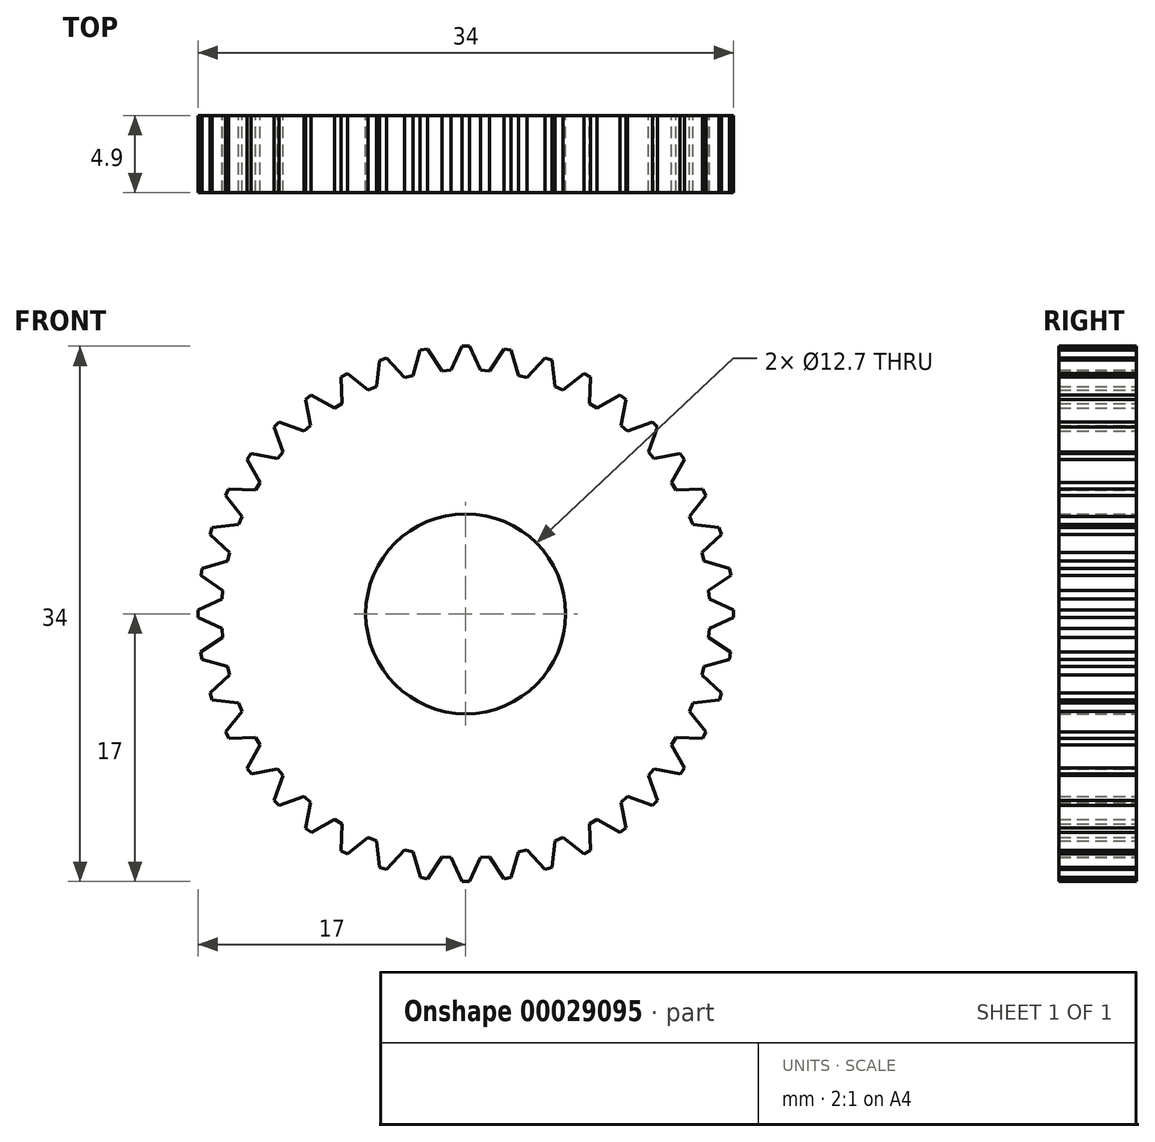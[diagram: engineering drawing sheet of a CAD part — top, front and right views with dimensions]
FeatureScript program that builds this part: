
annotation { "Feature Type Name" : "Feature", "Feature Type Description" : "" }
export const myFeature = defineFeature(function(context is Context, id is Id, definition is map)
    precondition{}
    {
        {
            var Q0;
            Q0=qCreatedBy(makeId("Front.planeOp"),FACE);
            var sketch = newSketch(context, id + "F0", { "sketchPlane" : qUnion([Q0])});
            skCircle(sketch, "E0", {"center": v(0, 0) * mm, "radius": 15 * mm, "construction": true});
            skCircle(sketch, "E1", {"center": v(0, 0) * mm, "radius": 15.5 * mm, "construction": true});
            skCircle(sketch, "E2", {"center": v(0, 0) * mm, "radius": 6.35 * mm});
            skCircle(sketch, "E3", {"center": v(0, 0) * mm, "radius": 17 * mm, "construction": true});
            skCircle(sketch, "E4", {"center": v(0, 0) * mm, "radius": 17.5 * mm, "construction": true});
            skLineSegment(sketch, "E5", {"start": v(0, 0) * mm, "end": v(0, 39.44) * mm, "construction": true});
            skLineSegment(sketch, "E6", {"start": v(0, 0) * mm, "end": v(-1.22, 15.45) * mm, "construction": true});
            skLineSegment(sketch, "E7", {"start": v(0, 0) * mm, "end": v(1.22, 15.45) * mm, "construction": true});
            skLineSegment(sketch, "E8", {"start": v(-0.94, 15.47) * mm, "end": v(-0.23, 17) * mm});
            skLineSegment(sketch, "E9", {"start": v(0.23, 17) * mm, "end": v(0.94, 15.47) * mm});
            skLineSegment(sketch, "E10", {"start": v(-1.22, 15.45) * mm, "end": v(-0.94, 15.47) * mm});
            skLineSegment(sketch, "E11", {"start": v(1.22, 15.45) * mm, "end": v(0.94, 15.47) * mm});
            skLineSegment(sketch, "E12", {"start": v(-0.23, 17) * mm, "end": v(0.23, 17) * mm});
            skLineSegment(sketch, "E13.1.0", {"start": v(-3.62, 15.07) * mm, "end": v(-3.35, 15.14) * mm});
            skLineSegment(sketch, "E13.1.1", {"start": v(-3.35, 15.13) * mm, "end": v(-2.89, 16.75) * mm});
            skLineSegment(sketch, "E13.1.2", {"start": v(-2.89, 16.75) * mm, "end": v(-2.43, 16.83) * mm});
            skLineSegment(sketch, "E13.1.3", {"start": v(-2.43, 16.83) * mm, "end": v(-1.5, 15.43) * mm});
            skLineSegment(sketch, "E13.1.4", {"start": v(-1.22, 15.45) * mm, "end": v(-1.5, 15.43) * mm});
            skLineSegment(sketch, "E13.2.0", {"start": v(-5.93, 14.32) * mm, "end": v(-5.67, 14.43) * mm});
            skLineSegment(sketch, "E13.2.1", {"start": v(-5.67, 14.42) * mm, "end": v(-5.47, 16.1) * mm});
            skLineSegment(sketch, "E13.2.2", {"start": v(-5.47, 16.1) * mm, "end": v(-5.04, 16.24) * mm});
            skLineSegment(sketch, "E13.2.3", {"start": v(-5.04, 16.24) * mm, "end": v(-3.89, 15) * mm});
            skLineSegment(sketch, "E13.2.4", {"start": v(-3.62, 15.07) * mm, "end": v(-3.9, 15) * mm});
            skLineSegment(sketch, "E13.3.0", {"start": v(-8.1, 13.22) * mm, "end": v(-7.86, 13.36) * mm});
            skLineSegment(sketch, "E13.3.1", {"start": v(-7.86, 13.36) * mm, "end": v(-7.92, 15.04) * mm});
            skLineSegment(sketch, "E13.3.2", {"start": v(-7.92, 15.04) * mm, "end": v(-7.52, 15.26) * mm});
            skLineSegment(sketch, "E13.3.3", {"start": v(-7.52, 15.26) * mm, "end": v(-6.19, 14.21) * mm});
            skLineSegment(sketch, "E13.3.4", {"start": v(-5.93, 14.32) * mm, "end": v(-6.2, 14.21) * mm});
            skLineSegment(sketch, "E13.4.0", {"start": v(-10.07, 11.79) * mm, "end": v(-9.85, 11.97) * mm});
            skLineSegment(sketch, "E13.4.1", {"start": v(-9.85, 11.97) * mm, "end": v(-10.18, 13.62) * mm});
            skLineSegment(sketch, "E13.4.2", {"start": v(-10.18, 13.62) * mm, "end": v(-9.8, 13.9) * mm});
            skLineSegment(sketch, "E13.4.3", {"start": v(-9.8, 13.9) * mm, "end": v(-8.34, 13.07) * mm});
            skLineSegment(sketch, "E13.4.4", {"start": v(-8.1, 13.22) * mm, "end": v(-8.34, 13.07) * mm});
            skLineSegment(sketch, "E13.5.0", {"start": v(-11.79, 10.07) * mm, "end": v(-11.6, 10.28) * mm});
            skLineSegment(sketch, "E13.5.1", {"start": v(-11.6, 10.28) * mm, "end": v(-12.18, 11.86) * mm});
            skLineSegment(sketch, "E13.5.2", {"start": v(-12.18, 11.86) * mm, "end": v(-11.86, 12.19) * mm});
            skLineSegment(sketch, "E13.5.3", {"start": v(-11.86, 12.19) * mm, "end": v(-10.28, 11.6) * mm});
            skLineSegment(sketch, "E13.5.4", {"start": v(-10.07, 11.79) * mm, "end": v(-10.28, 11.6) * mm});
            skLineSegment(sketch, "E13.6.0", {"start": v(-13.22, 8.1) * mm, "end": v(-13.07, 8.34) * mm});
            skLineSegment(sketch, "E13.6.1", {"start": v(-13.07, 8.34) * mm, "end": v(-13.89, 9.8) * mm});
            skLineSegment(sketch, "E13.6.2", {"start": v(-13.89, 9.8) * mm, "end": v(-13.62, 10.18) * mm});
            skLineSegment(sketch, "E13.6.3", {"start": v(-13.62, 10.18) * mm, "end": v(-11.97, 9.85) * mm});
            skLineSegment(sketch, "E13.6.4", {"start": v(-11.79, 10.07) * mm, "end": v(-11.97, 9.85) * mm});
            skLineSegment(sketch, "E13.7.0", {"start": v(-14.32, 5.93) * mm, "end": v(-14.21, 6.2) * mm});
            skLineSegment(sketch, "E13.7.1", {"start": v(-14.21, 6.19) * mm, "end": v(-15.25, 7.51) * mm});
            skLineSegment(sketch, "E13.7.2", {"start": v(-15.25, 7.51) * mm, "end": v(-15.05, 7.92) * mm});
            skLineSegment(sketch, "E13.7.3", {"start": v(-15.05, 7.92) * mm, "end": v(-13.36, 7.86) * mm});
            skLineSegment(sketch, "E13.7.4", {"start": v(-13.22, 8.1) * mm, "end": v(-13.36, 7.86) * mm});
            skLineSegment(sketch, "E13.8.0", {"start": v(-15.07, 3.62) * mm, "end": v(-15, 3.9) * mm});
            skLineSegment(sketch, "E13.8.1", {"start": v(-15, 3.89) * mm, "end": v(-16.24, 5.03) * mm});
            skLineSegment(sketch, "E13.8.2", {"start": v(-16.24, 5.03) * mm, "end": v(-16.1, 5.47) * mm});
            skLineSegment(sketch, "E13.8.3", {"start": v(-16.1, 5.47) * mm, "end": v(-14.42, 5.67) * mm});
            skLineSegment(sketch, "E13.8.4", {"start": v(-14.32, 5.93) * mm, "end": v(-14.43, 5.67) * mm});
            skLineSegment(sketch, "E13.9.0", {"start": v(-15.45, 1.22) * mm, "end": v(-15.43, 1.5) * mm});
            skLineSegment(sketch, "E13.9.1", {"start": v(-15.43, 1.5) * mm, "end": v(-16.83, 2.43) * mm});
            skLineSegment(sketch, "E13.9.2", {"start": v(-16.83, 2.43) * mm, "end": v(-16.76, 2.89) * mm});
            skLineSegment(sketch, "E13.9.3", {"start": v(-16.76, 2.89) * mm, "end": v(-15.13, 3.35) * mm});
            skLineSegment(sketch, "E13.9.4", {"start": v(-15.07, 3.62) * mm, "end": v(-15.14, 3.35) * mm});
            skLineSegment(sketch, "E13.10.0", {"start": v(-15.45, -1.22) * mm, "end": v(-15.47, -0.94) * mm});
            skLineSegment(sketch, "E13.10.1", {"start": v(-15.47, -0.94) * mm, "end": v(-17, -0.23) * mm});
            skLineSegment(sketch, "E13.10.2", {"start": v(-17, -0.23) * mm, "end": v(-17, 0.23) * mm});
            skLineSegment(sketch, "E13.10.3", {"start": v(-17, 0.23) * mm, "end": v(-15.47, 0.94) * mm});
            skLineSegment(sketch, "E13.10.4", {"start": v(-15.45, 1.22) * mm, "end": v(-15.47, 0.94) * mm});
            skLineSegment(sketch, "E13.11.0", {"start": v(-15.07, -3.62) * mm, "end": v(-15.14, -3.35) * mm});
            skLineSegment(sketch, "E13.11.1", {"start": v(-15.13, -3.35) * mm, "end": v(-16.75, -2.89) * mm});
            skLineSegment(sketch, "E13.11.2", {"start": v(-16.75, -2.89) * mm, "end": v(-16.83, -2.43) * mm});
            skLineSegment(sketch, "E13.11.3", {"start": v(-16.83, -2.43) * mm, "end": v(-15.43, -1.5) * mm});
            skLineSegment(sketch, "E13.11.4", {"start": v(-15.45, -1.22) * mm, "end": v(-15.43, -1.5) * mm});
            skLineSegment(sketch, "E13.12.0", {"start": v(-14.32, -5.93) * mm, "end": v(-14.43, -5.67) * mm});
            skLineSegment(sketch, "E13.12.1", {"start": v(-14.42, -5.67) * mm, "end": v(-16.1, -5.47) * mm});
            skLineSegment(sketch, "E13.12.2", {"start": v(-16.1, -5.47) * mm, "end": v(-16.24, -5.04) * mm});
            skLineSegment(sketch, "E13.12.3", {"start": v(-16.24, -5.04) * mm, "end": v(-15, -3.89) * mm});
            skLineSegment(sketch, "E13.12.4", {"start": v(-15.07, -3.62) * mm, "end": v(-15, -3.9) * mm});
            skLineSegment(sketch, "E13.13.0", {"start": v(-13.22, -8.1) * mm, "end": v(-13.36, -7.86) * mm});
            skLineSegment(sketch, "E13.13.1", {"start": v(-13.36, -7.86) * mm, "end": v(-15.04, -7.92) * mm});
            skLineSegment(sketch, "E13.13.2", {"start": v(-15.04, -7.92) * mm, "end": v(-15.26, -7.52) * mm});
            skLineSegment(sketch, "E13.13.3", {"start": v(-15.26, -7.52) * mm, "end": v(-14.21, -6.19) * mm});
            skLineSegment(sketch, "E13.13.4", {"start": v(-14.32, -5.93) * mm, "end": v(-14.21, -6.2) * mm});
            skLineSegment(sketch, "E13.14.0", {"start": v(-11.79, -10.07) * mm, "end": v(-11.97, -9.85) * mm});
            skLineSegment(sketch, "E13.14.1", {"start": v(-11.97, -9.85) * mm, "end": v(-13.62, -10.18) * mm});
            skLineSegment(sketch, "E13.14.2", {"start": v(-13.62, -10.18) * mm, "end": v(-13.9, -9.8) * mm});
            skLineSegment(sketch, "E13.14.3", {"start": v(-13.9, -9.8) * mm, "end": v(-13.07, -8.34) * mm});
            skLineSegment(sketch, "E13.14.4", {"start": v(-13.22, -8.1) * mm, "end": v(-13.07, -8.34) * mm});
            skLineSegment(sketch, "E13.15.0", {"start": v(-10.07, -11.79) * mm, "end": v(-10.28, -11.6) * mm});
            skLineSegment(sketch, "E13.15.1", {"start": v(-10.28, -11.6) * mm, "end": v(-11.86, -12.18) * mm});
            skLineSegment(sketch, "E13.15.2", {"start": v(-11.86, -12.18) * mm, "end": v(-12.19, -11.86) * mm});
            skLineSegment(sketch, "E13.15.3", {"start": v(-12.19, -11.86) * mm, "end": v(-11.6, -10.28) * mm});
            skLineSegment(sketch, "E13.15.4", {"start": v(-11.79, -10.07) * mm, "end": v(-11.6, -10.28) * mm});
            skLineSegment(sketch, "E13.16.0", {"start": v(-8.1, -13.22) * mm, "end": v(-8.34, -13.07) * mm});
            skLineSegment(sketch, "E13.16.1", {"start": v(-8.34, -13.07) * mm, "end": v(-9.8, -13.89) * mm});
            skLineSegment(sketch, "E13.16.2", {"start": v(-9.8, -13.89) * mm, "end": v(-10.18, -13.62) * mm});
            skLineSegment(sketch, "E13.16.3", {"start": v(-10.18, -13.62) * mm, "end": v(-9.85, -11.97) * mm});
            skLineSegment(sketch, "E13.16.4", {"start": v(-10.07, -11.79) * mm, "end": v(-9.85, -11.97) * mm});
            skLineSegment(sketch, "E13.17.0", {"start": v(-5.93, -14.32) * mm, "end": v(-6.2, -14.21) * mm});
            skLineSegment(sketch, "E13.17.1", {"start": v(-6.19, -14.21) * mm, "end": v(-7.51, -15.25) * mm});
            skLineSegment(sketch, "E13.17.2", {"start": v(-7.51, -15.25) * mm, "end": v(-7.92, -15.05) * mm});
            skLineSegment(sketch, "E13.17.3", {"start": v(-7.92, -15.05) * mm, "end": v(-7.86, -13.36) * mm});
            skLineSegment(sketch, "E13.17.4", {"start": v(-8.1, -13.22) * mm, "end": v(-7.86, -13.36) * mm});
            skLineSegment(sketch, "E13.18.0", {"start": v(-3.62, -15.07) * mm, "end": v(-3.9, -15) * mm});
            skLineSegment(sketch, "E13.18.1", {"start": v(-3.89, -15) * mm, "end": v(-5.03, -16.24) * mm});
            skLineSegment(sketch, "E13.18.2", {"start": v(-5.03, -16.24) * mm, "end": v(-5.47, -16.1) * mm});
            skLineSegment(sketch, "E13.18.3", {"start": v(-5.47, -16.1) * mm, "end": v(-5.67, -14.42) * mm});
            skLineSegment(sketch, "E13.18.4", {"start": v(-5.93, -14.32) * mm, "end": v(-5.67, -14.43) * mm});
            skLineSegment(sketch, "E13.19.0", {"start": v(-1.22, -15.45) * mm, "end": v(-1.5, -15.43) * mm});
            skLineSegment(sketch, "E13.19.1", {"start": v(-1.5, -15.43) * mm, "end": v(-2.43, -16.83) * mm});
            skLineSegment(sketch, "E13.19.2", {"start": v(-2.43, -16.83) * mm, "end": v(-2.89, -16.76) * mm});
            skLineSegment(sketch, "E13.19.3", {"start": v(-2.89, -16.76) * mm, "end": v(-3.35, -15.13) * mm});
            skLineSegment(sketch, "E13.19.4", {"start": v(-3.62, -15.07) * mm, "end": v(-3.35, -15.14) * mm});
            skLineSegment(sketch, "E13.20.0", {"start": v(1.22, -15.45) * mm, "end": v(0.94, -15.47) * mm});
            skLineSegment(sketch, "E13.20.1", {"start": v(0.94, -15.47) * mm, "end": v(0.23, -17) * mm});
            skLineSegment(sketch, "E13.20.2", {"start": v(0.23, -17) * mm, "end": v(-0.23, -17) * mm});
            skLineSegment(sketch, "E13.20.3", {"start": v(-0.23, -17) * mm, "end": v(-0.94, -15.47) * mm});
            skLineSegment(sketch, "E13.20.4", {"start": v(-1.22, -15.45) * mm, "end": v(-0.94, -15.47) * mm});
            skLineSegment(sketch, "E13.21.0", {"start": v(3.62, -15.07) * mm, "end": v(3.35, -15.14) * mm});
            skLineSegment(sketch, "E13.21.1", {"start": v(3.35, -15.13) * mm, "end": v(2.89, -16.75) * mm});
            skLineSegment(sketch, "E13.21.2", {"start": v(2.89, -16.75) * mm, "end": v(2.43, -16.83) * mm});
            skLineSegment(sketch, "E13.21.3", {"start": v(2.43, -16.83) * mm, "end": v(1.5, -15.43) * mm});
            skLineSegment(sketch, "E13.21.4", {"start": v(1.22, -15.45) * mm, "end": v(1.5, -15.43) * mm});
            skLineSegment(sketch, "E13.22.0", {"start": v(5.93, -14.32) * mm, "end": v(5.67, -14.43) * mm});
            skLineSegment(sketch, "E13.22.1", {"start": v(5.67, -14.42) * mm, "end": v(5.47, -16.1) * mm});
            skLineSegment(sketch, "E13.22.2", {"start": v(5.47, -16.1) * mm, "end": v(5.04, -16.24) * mm});
            skLineSegment(sketch, "E13.22.3", {"start": v(5.04, -16.24) * mm, "end": v(3.89, -15) * mm});
            skLineSegment(sketch, "E13.22.4", {"start": v(3.62, -15.07) * mm, "end": v(3.9, -15) * mm});
            skLineSegment(sketch, "E13.23.0", {"start": v(8.1, -13.22) * mm, "end": v(7.86, -13.36) * mm});
            skLineSegment(sketch, "E13.23.1", {"start": v(7.86, -13.36) * mm, "end": v(7.92, -15.04) * mm});
            skLineSegment(sketch, "E13.23.2", {"start": v(7.92, -15.04) * mm, "end": v(7.52, -15.26) * mm});
            skLineSegment(sketch, "E13.23.3", {"start": v(7.52, -15.26) * mm, "end": v(6.19, -14.21) * mm});
            skLineSegment(sketch, "E13.23.4", {"start": v(5.93, -14.32) * mm, "end": v(6.2, -14.21) * mm});
            skLineSegment(sketch, "E13.24.0", {"start": v(10.07, -11.79) * mm, "end": v(9.85, -11.97) * mm});
            skLineSegment(sketch, "E13.24.1", {"start": v(9.85, -11.97) * mm, "end": v(10.18, -13.62) * mm});
            skLineSegment(sketch, "E13.24.2", {"start": v(10.18, -13.62) * mm, "end": v(9.8, -13.9) * mm});
            skLineSegment(sketch, "E13.24.3", {"start": v(9.8, -13.9) * mm, "end": v(8.34, -13.07) * mm});
            skLineSegment(sketch, "E13.24.4", {"start": v(8.1, -13.22) * mm, "end": v(8.34, -13.07) * mm});
            skLineSegment(sketch, "E13.25.0", {"start": v(11.79, -10.07) * mm, "end": v(11.6, -10.28) * mm});
            skLineSegment(sketch, "E13.25.1", {"start": v(11.6, -10.28) * mm, "end": v(12.18, -11.86) * mm});
            skLineSegment(sketch, "E13.25.2", {"start": v(12.18, -11.86) * mm, "end": v(11.86, -12.19) * mm});
            skLineSegment(sketch, "E13.25.3", {"start": v(11.86, -12.19) * mm, "end": v(10.28, -11.6) * mm});
            skLineSegment(sketch, "E13.25.4", {"start": v(10.07, -11.79) * mm, "end": v(10.28, -11.6) * mm});
            skLineSegment(sketch, "E13.26.0", {"start": v(13.22, -8.1) * mm, "end": v(13.07, -8.34) * mm});
            skLineSegment(sketch, "E13.26.1", {"start": v(13.07, -8.34) * mm, "end": v(13.89, -9.8) * mm});
            skLineSegment(sketch, "E13.26.2", {"start": v(13.89, -9.8) * mm, "end": v(13.62, -10.18) * mm});
            skLineSegment(sketch, "E13.26.3", {"start": v(13.62, -10.18) * mm, "end": v(11.97, -9.85) * mm});
            skLineSegment(sketch, "E13.26.4", {"start": v(11.79, -10.07) * mm, "end": v(11.97, -9.85) * mm});
            skLineSegment(sketch, "E13.27.0", {"start": v(14.32, -5.93) * mm, "end": v(14.21, -6.2) * mm});
            skLineSegment(sketch, "E13.27.1", {"start": v(14.21, -6.19) * mm, "end": v(15.25, -7.51) * mm});
            skLineSegment(sketch, "E13.27.2", {"start": v(15.25, -7.51) * mm, "end": v(15.05, -7.92) * mm});
            skLineSegment(sketch, "E13.27.3", {"start": v(15.05, -7.92) * mm, "end": v(13.36, -7.86) * mm});
            skLineSegment(sketch, "E13.27.4", {"start": v(13.22, -8.1) * mm, "end": v(13.36, -7.86) * mm});
            skLineSegment(sketch, "E13.28.0", {"start": v(15.07, -3.62) * mm, "end": v(15, -3.9) * mm});
            skLineSegment(sketch, "E13.28.1", {"start": v(15, -3.89) * mm, "end": v(16.24, -5.03) * mm});
            skLineSegment(sketch, "E13.28.2", {"start": v(16.24, -5.03) * mm, "end": v(16.1, -5.47) * mm});
            skLineSegment(sketch, "E13.28.3", {"start": v(16.1, -5.47) * mm, "end": v(14.42, -5.67) * mm});
            skLineSegment(sketch, "E13.28.4", {"start": v(14.32, -5.93) * mm, "end": v(14.43, -5.67) * mm});
            skLineSegment(sketch, "E13.29.0", {"start": v(15.45, -1.22) * mm, "end": v(15.43, -1.5) * mm});
            skLineSegment(sketch, "E13.29.1", {"start": v(15.43, -1.5) * mm, "end": v(16.83, -2.43) * mm});
            skLineSegment(sketch, "E13.29.2", {"start": v(16.83, -2.43) * mm, "end": v(16.76, -2.89) * mm});
            skLineSegment(sketch, "E13.29.3", {"start": v(16.76, -2.89) * mm, "end": v(15.13, -3.35) * mm});
            skLineSegment(sketch, "E13.29.4", {"start": v(15.07, -3.62) * mm, "end": v(15.14, -3.35) * mm});
            skLineSegment(sketch, "E13.30.0", {"start": v(15.45, 1.22) * mm, "end": v(15.47, 0.94) * mm});
            skLineSegment(sketch, "E13.30.1", {"start": v(15.47, 0.94) * mm, "end": v(17, 0.23) * mm});
            skLineSegment(sketch, "E13.30.2", {"start": v(17, 0.23) * mm, "end": v(17, -0.23) * mm});
            skLineSegment(sketch, "E13.30.3", {"start": v(17, -0.23) * mm, "end": v(15.47, -0.94) * mm});
            skLineSegment(sketch, "E13.30.4", {"start": v(15.45, -1.22) * mm, "end": v(15.47, -0.94) * mm});
            skLineSegment(sketch, "E13.31.0", {"start": v(15.07, 3.62) * mm, "end": v(15.14, 3.35) * mm});
            skLineSegment(sketch, "E13.31.1", {"start": v(15.13, 3.35) * mm, "end": v(16.75, 2.89) * mm});
            skLineSegment(sketch, "E13.31.2", {"start": v(16.75, 2.89) * mm, "end": v(16.83, 2.43) * mm});
            skLineSegment(sketch, "E13.31.3", {"start": v(16.83, 2.43) * mm, "end": v(15.43, 1.5) * mm});
            skLineSegment(sketch, "E13.31.4", {"start": v(15.45, 1.22) * mm, "end": v(15.43, 1.5) * mm});
            skLineSegment(sketch, "E13.32.0", {"start": v(14.32, 5.93) * mm, "end": v(14.43, 5.67) * mm});
            skLineSegment(sketch, "E13.32.1", {"start": v(14.42, 5.67) * mm, "end": v(16.1, 5.47) * mm});
            skLineSegment(sketch, "E13.32.2", {"start": v(16.1, 5.47) * mm, "end": v(16.24, 5.04) * mm});
            skLineSegment(sketch, "E13.32.3", {"start": v(16.24, 5.04) * mm, "end": v(15, 3.89) * mm});
            skLineSegment(sketch, "E13.32.4", {"start": v(15.07, 3.62) * mm, "end": v(15, 3.9) * mm});
            skLineSegment(sketch, "E13.33.0", {"start": v(13.22, 8.1) * mm, "end": v(13.36, 7.86) * mm});
            skLineSegment(sketch, "E13.33.1", {"start": v(13.36, 7.86) * mm, "end": v(15.04, 7.92) * mm});
            skLineSegment(sketch, "E13.33.2", {"start": v(15.04, 7.92) * mm, "end": v(15.26, 7.52) * mm});
            skLineSegment(sketch, "E13.33.3", {"start": v(15.26, 7.52) * mm, "end": v(14.21, 6.19) * mm});
            skLineSegment(sketch, "E13.33.4", {"start": v(14.32, 5.93) * mm, "end": v(14.21, 6.2) * mm});
            skLineSegment(sketch, "E13.34.0", {"start": v(11.79, 10.07) * mm, "end": v(11.97, 9.85) * mm});
            skLineSegment(sketch, "E13.34.1", {"start": v(11.97, 9.85) * mm, "end": v(13.62, 10.18) * mm});
            skLineSegment(sketch, "E13.34.2", {"start": v(13.62, 10.18) * mm, "end": v(13.9, 9.8) * mm});
            skLineSegment(sketch, "E13.34.3", {"start": v(13.9, 9.8) * mm, "end": v(13.07, 8.34) * mm});
            skLineSegment(sketch, "E13.34.4", {"start": v(13.22, 8.1) * mm, "end": v(13.07, 8.34) * mm});
            skLineSegment(sketch, "E13.35.0", {"start": v(10.07, 11.79) * mm, "end": v(10.28, 11.6) * mm});
            skLineSegment(sketch, "E13.35.1", {"start": v(10.28, 11.6) * mm, "end": v(11.86, 12.18) * mm});
            skLineSegment(sketch, "E13.35.2", {"start": v(11.86, 12.18) * mm, "end": v(12.19, 11.86) * mm});
            skLineSegment(sketch, "E13.35.3", {"start": v(12.19, 11.86) * mm, "end": v(11.6, 10.28) * mm});
            skLineSegment(sketch, "E13.35.4", {"start": v(11.79, 10.07) * mm, "end": v(11.6, 10.28) * mm});
            skLineSegment(sketch, "E13.36.0", {"start": v(8.1, 13.22) * mm, "end": v(8.34, 13.07) * mm});
            skLineSegment(sketch, "E13.36.1", {"start": v(8.34, 13.07) * mm, "end": v(9.8, 13.89) * mm});
            skLineSegment(sketch, "E13.36.2", {"start": v(9.8, 13.89) * mm, "end": v(10.18, 13.62) * mm});
            skLineSegment(sketch, "E13.36.3", {"start": v(10.18, 13.62) * mm, "end": v(9.85, 11.97) * mm});
            skLineSegment(sketch, "E13.36.4", {"start": v(10.07, 11.79) * mm, "end": v(9.85, 11.97) * mm});
            skLineSegment(sketch, "E13.37.0", {"start": v(5.93, 14.32) * mm, "end": v(6.2, 14.21) * mm});
            skLineSegment(sketch, "E13.37.1", {"start": v(6.19, 14.21) * mm, "end": v(7.51, 15.25) * mm});
            skLineSegment(sketch, "E13.37.2", {"start": v(7.51, 15.25) * mm, "end": v(7.92, 15.05) * mm});
            skLineSegment(sketch, "E13.37.3", {"start": v(7.92, 15.05) * mm, "end": v(7.86, 13.36) * mm});
            skLineSegment(sketch, "E13.37.4", {"start": v(8.1, 13.22) * mm, "end": v(7.86, 13.36) * mm});
            skLineSegment(sketch, "E13.38.0", {"start": v(3.62, 15.07) * mm, "end": v(3.9, 15) * mm});
            skLineSegment(sketch, "E13.38.1", {"start": v(3.89, 15) * mm, "end": v(5.03, 16.24) * mm});
            skLineSegment(sketch, "E13.38.2", {"start": v(5.03, 16.24) * mm, "end": v(5.47, 16.1) * mm});
            skLineSegment(sketch, "E13.38.3", {"start": v(5.47, 16.1) * mm, "end": v(5.67, 14.42) * mm});
            skLineSegment(sketch, "E13.38.4", {"start": v(5.93, 14.32) * mm, "end": v(5.67, 14.43) * mm});
            skLineSegment(sketch, "E13.39.0", {"start": v(1.22, 15.45) * mm, "end": v(1.5, 15.43) * mm});
            skLineSegment(sketch, "E13.39.1", {"start": v(1.5, 15.43) * mm, "end": v(2.43, 16.83) * mm});
            skLineSegment(sketch, "E13.39.2", {"start": v(2.43, 16.83) * mm, "end": v(2.89, 16.76) * mm});
            skLineSegment(sketch, "E13.39.3", {"start": v(2.89, 16.76) * mm, "end": v(3.35, 15.13) * mm});
            skLineSegment(sketch, "E13.39.4", {"start": v(3.62, 15.07) * mm, "end": v(3.35, 15.14) * mm});
            skSolve(sketch);
        }
        {
            var Q0;
            Q0=makeQuery(id+"F0.imprint","IMPRINT",FACE,{"disambiguationData":[TD([[makeQuery(id+"F0.imprint","IMPRINT",EDGE,{"derivedFrom":sQuery(id+"F0.wireOp",EDGE,"E2")}),-1.0]])]});
            extrude(context, id + "F1", {"entities" : qUnion([Q0]), "depth" : 4.9 * mm});
        }
    });
